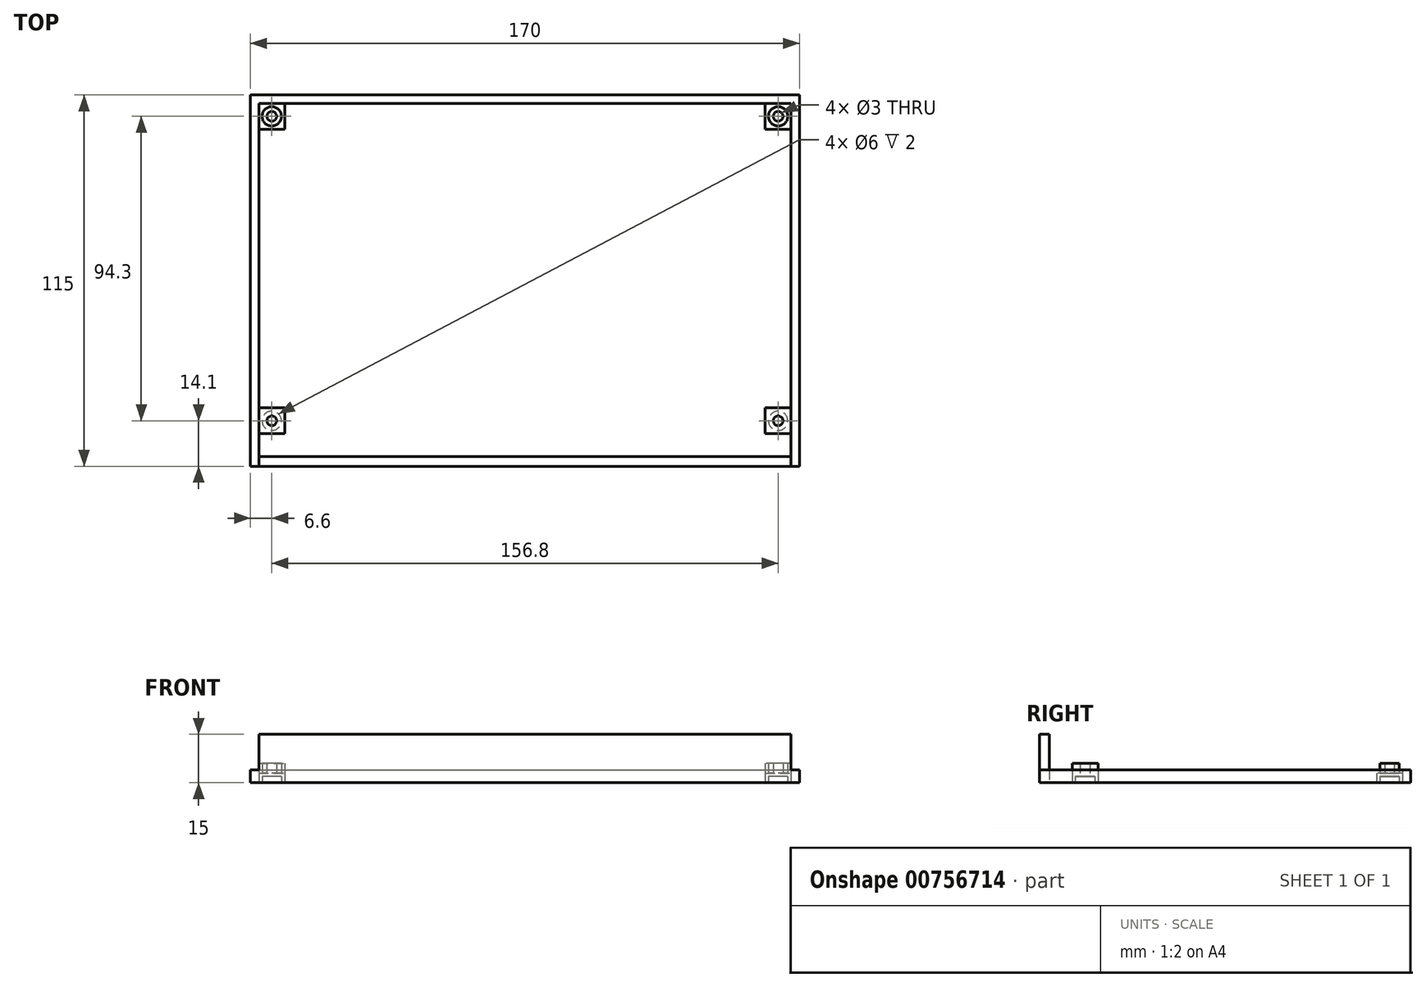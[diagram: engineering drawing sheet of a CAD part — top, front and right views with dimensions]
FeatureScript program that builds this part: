
annotation { "Feature Type Name" : "Feature", "Feature Type Description" : "" }
export const myFeature = defineFeature(function(context is Context, id is Id, definition is map)
    precondition{}
    {
        {
            var Q0;
            Q0=qCreatedBy(makeId("Top.planeOp"),FACE);
            var sketch = newSketch(context, id + "F0", { "sketchPlane" : qUnion([Q0])});
            skLineSegment(sketch, "E0.bottom", {"start": v(0, 0) * mm, "end": v(170, 0) * mm});
            skLineSegment(sketch, "E0.top", {"start": v(0, -115) * mm, "end": v(170, -115) * mm});
            skLineSegment(sketch, "E0.left", {"start": v(0, 0) * mm, "end": v(0, -115) * mm});
            skLineSegment(sketch, "E0.right", {"start": v(170, 0) * mm, "end": v(170, -115) * mm});
            skLineSegment(sketch, "E1", {"start": v(2.6, -115) * mm, "end": v(2.6, -2.6) * mm});
            skLineSegment(sketch, "E2", {"start": v(2.6, -2.6) * mm, "end": v(167.4, -2.6) * mm});
            skLineSegment(sketch, "E3", {"start": v(167.4, -2.6) * mm, "end": v(167.4, -115) * mm});
            skLineSegment(sketch, "E4", {"start": v(0, -67.06) * mm, "end": v(2.6, -67.06) * mm, "construction": true});
            skLineSegment(sketch, "E5", {"start": v(77.9, -2.6) * mm, "end": v(77.9, 0) * mm, "construction": true});
            skLineSegment(sketch, "E6", {"start": v(167.4, -63.68) * mm, "end": v(170, -63.68) * mm, "construction": true});
            skLineSegment(sketch, "E7.bottom", {"start": v(2.6, -2.6) * mm, "end": v(10.6, -2.6) * mm});
            skLineSegment(sketch, "E7.top", {"start": v(2.6, -10.6) * mm, "end": v(10.6, -10.6) * mm});
            skLineSegment(sketch, "E7.left", {"start": v(2.6, -2.6) * mm, "end": v(2.6, -10.6) * mm});
            skLineSegment(sketch, "E7.right", {"start": v(10.6, -2.6) * mm, "end": v(10.6, -10.6) * mm});
            skLineSegment(sketch, "E8.bottom", {"start": v(167.4, -2.6) * mm, "end": v(159.4, -2.6) * mm});
            skLineSegment(sketch, "E8.top", {"start": v(167.4, -10.6) * mm, "end": v(159.4, -10.6) * mm});
            skLineSegment(sketch, "E8.left", {"start": v(167.4, -2.6) * mm, "end": v(167.4, -10.6) * mm});
            skLineSegment(sketch, "E8.right", {"start": v(159.4, -2.6) * mm, "end": v(159.4, -10.6) * mm});
            skLineSegment(sketch, "E9.bottom", {"start": v(167.4, -96.9) * mm, "end": v(159.4, -96.9) * mm});
            skLineSegment(sketch, "E9.top", {"start": v(167.4, -104.9) * mm, "end": v(159.4, -104.9) * mm});
            skLineSegment(sketch, "E9.left", {"start": v(167.4, -96.9) * mm, "end": v(167.4, -104.9) * mm});
            skLineSegment(sketch, "E9.right", {"start": v(159.4, -96.9) * mm, "end": v(159.4, -104.9) * mm});
            skLineSegment(sketch, "E10.bottom", {"start": v(2.6, -96.9) * mm, "end": v(10.6, -96.9) * mm});
            skLineSegment(sketch, "E10.top", {"start": v(2.6, -104.9) * mm, "end": v(10.6, -104.9) * mm});
            skLineSegment(sketch, "E10.left", {"start": v(2.6, -96.9) * mm, "end": v(2.6, -104.9) * mm});
            skLineSegment(sketch, "E10.right", {"start": v(10.6, -96.9) * mm, "end": v(10.6, -104.9) * mm});
            skLineSegment(sketch, "E11", {"start": v(2.6, -112) * mm, "end": v(167.4, -112) * mm});
            skLineSegment(sketch, "E12", {"start": v(167.4, -112) * mm, "end": v(167.4, -115) * mm});
            skLineSegment(sketch, "E13", {"start": v(2.6, -115) * mm, "end": v(2.6, -112) * mm});
            skLineSegment(sketch, "E14", {"start": v(2.6, -2.6) * mm, "end": v(10.6, -10.6) * mm, "construction": true});
            skLineSegment(sketch, "E15", {"start": v(159.4, -2.6) * mm, "end": v(167.4, -10.6) * mm, "construction": true});
            skLineSegment(sketch, "E16", {"start": v(159.4, -96.9) * mm, "end": v(167.4, -104.9) * mm, "construction": true});
            skLineSegment(sketch, "E17", {"start": v(2.6, -96.9) * mm, "end": v(10.6, -104.9) * mm, "construction": true});
            skCircle(sketch, "E18", {"center": v(6.6, -6.6) * mm, "radius": 1.5 * mm});
            skCircle(sketch, "E19", {"center": v(163.4, -6.6) * mm, "radius": 1.5 * mm});
            skCircle(sketch, "E20", {"center": v(163.4, -100.9) * mm, "radius": 1.5 * mm});
            skCircle(sketch, "E21", {"center": v(6.6, -100.9) * mm, "radius": 1.5 * mm});
            skCircle(sketch, "E22", {"center": v(163.4, -6.6) * mm, "radius": 3 * mm});
            skCircle(sketch, "E23", {"center": v(6.6, -6.6) * mm, "radius": 3 * mm});
            skCircle(sketch, "E24", {"center": v(6.6, -100.9) * mm, "radius": 3 * mm});
            skCircle(sketch, "E25", {"center": v(163.4, -100.9) * mm, "radius": 3 * mm});
            skSolve(sketch);
        }
        {
            var Q0;
            Q0=makeQuery(id+"F0.imprint","IMPRINT",FACE,{"disambiguationData":[TD([[makeQuery(id+"F0.imprint","IMPRINT",EDGE,{"derivedFrom":sQuery(id+"F0.wireOp",EDGE,"E0.bottom")}),-1.0]])]});
            extrude(context, id + "F1", {"entities" : qUnion([Q0]), "depth" : 4 * mm, "offsetDistance" : 25 * mm});
        }
        {
            var Q0;
            Q0=makeQuery(id+"F0.imprint","IMPRINT",FACE,{"disambiguationData":[TD([[makeQuery(id+"F0.imprint","IMPRINT",EDGE,{"derivedFrom":sQuery(id+"F0.wireOp",EDGE,"E2")}),-1.0]])]});
            extrude(context, id + "F2", {"entities" : qUnion([Q0]), "operationType" : NewBodyOperationType.ADD, "depth" : 3 * mm, "offsetDistance" : 25 * mm});
        }
        {
            var Q0;
            Q0=makeQuery(id+"F0.imprint","IMPRINT",FACE,{"disambiguationData":[TD([[makeQuery(id+"F0.imprint","IMPRINT",EDGE,{"derivedFrom":sQuery(id+"F0.wireOp",EDGE,"E10.bottom")}),-1.0]])]});
            var Q1;
            Q1=makeQuery(id+"F0.imprint","IMPRINT",FACE,{"disambiguationData":[TD([[makeQuery(id+"F0.imprint","IMPRINT",EDGE,{"derivedFrom":sQuery(id+"F0.wireOp",EDGE,"E21")}),-1.0]])]});
            var Q2;
            Q2=makeQuery(id+"F0.imprint","IMPRINT",FACE,{"disambiguationData":[TD([[makeQuery(id+"F0.imprint","IMPRINT",EDGE,{"derivedFrom":sQuery(id+"F0.wireOp",EDGE,"E9.bottom")}),1.0]])]});
            var Q3;
            Q3=makeQuery(id+"F0.imprint","IMPRINT",FACE,{"disambiguationData":[TD([[makeQuery(id+"F0.imprint","IMPRINT",EDGE,{"derivedFrom":sQuery(id+"F0.wireOp",EDGE,"E20")}),-1.0]])]});
            var Q4;
            Q4=makeQuery(id+"F0.imprint","IMPRINT",FACE,{"disambiguationData":[TD([[makeQuery(id+"F0.imprint","IMPRINT",EDGE,{"derivedFrom":sQuery(id+"F0.wireOp",EDGE,"E8.bottom")}),1.0]])]});
            var Q5;
            Q5=makeQuery(id+"F0.imprint","IMPRINT",FACE,{"disambiguationData":[TD([[makeQuery(id+"F0.imprint","IMPRINT",EDGE,{"derivedFrom":sQuery(id+"F0.wireOp",EDGE,"E19")}),-1.0]])]});
            var Q6;
            Q6=makeQuery(id+"F0.imprint","IMPRINT",FACE,{"disambiguationData":[TD([[makeQuery(id+"F0.imprint","IMPRINT",EDGE,{"derivedFrom":sQuery(id+"F0.wireOp",EDGE,"E7.bottom")}),-1.0]])]});
            var Q7;
            Q7=makeQuery(id+"F0.imprint","IMPRINT",FACE,{"disambiguationData":[TD([[makeQuery(id+"F0.imprint","IMPRINT",EDGE,{"derivedFrom":sQuery(id+"F0.wireOp",EDGE,"E18")}),-1.0]])]});
            extrude(context, id + "F3", {"entities" : qUnion([Q0, Q1, Q2, Q3, Q4, Q5, Q6, Q7]), "operationType" : NewBodyOperationType.ADD, "depth" : 6 * mm, "offsetDistance" : 25 * mm});
        }
        {
            var Q0;
            Q0=makeQuery(id+"F0.imprint","IMPRINT",FACE,{"disambiguationData":[TD([[makeQuery(id+"F0.imprint","IMPRINT",EDGE,{"derivedFrom":sQuery(id+"F0.wireOp",EDGE,"E11")}),-1.0]])]});
            extrude(context, id + "F4", {"entities" : qUnion([Q0]), "operationType" : NewBodyOperationType.ADD, "depth" : 15 * mm, "offsetDistance" : 25 * mm});
        }
        {
            var Q0;
            Q0=makeQuery(id+"F0.imprint","IMPRINT",FACE,{"disambiguationData":[TD([[makeQuery(id+"F0.imprint","IMPRINT",EDGE,{"derivedFrom":sQuery(id+"F0.wireOp",EDGE,"E19")}),-1.0]])]});
            var Q1;
            Q1=makeQuery(id+"F0.imprint","IMPRINT",FACE,{"disambiguationData":[TD([[makeQuery(id+"F0.imprint","IMPRINT",EDGE,{"derivedFrom":sQuery(id+"F0.wireOp",EDGE,"E18")}),-1.0]])]});
            var Q2;
            Q2=makeQuery(id+"F0.imprint","IMPRINT",FACE,{"disambiguationData":[TD([[makeQuery(id+"F0.imprint","IMPRINT",EDGE,{"derivedFrom":sQuery(id+"F0.wireOp",EDGE,"E21")}),-1.0]])]});
            var Q3;
            Q3=makeQuery(id+"F0.imprint","IMPRINT",FACE,{"disambiguationData":[TD([[makeQuery(id+"F0.imprint","IMPRINT",EDGE,{"derivedFrom":sQuery(id+"F0.wireOp",EDGE,"E20")}),-1.0]])]});
            extrude(context, id + "F5", {"entities" : qUnion([Q0, Q1, Q2, Q3]), "operationType" : NewBodyOperationType.REMOVE, "depth" : 2 * mm, "offsetDistance" : 25 * mm});
        }
        {
            var Q0;
            {var subQ0=sQuery(id+"F0.wireOp",EDGE,"E13");var subQ1=sQuery(id+"F0.wireOp",EDGE,"E12");var subQ2=sQuery(id+"F0.wireOp",EDGE,"E11");var subQ3=sQuery(id+"F0.wireOp",EDGE,"E0.top");var subQ4=sQuery(id+"F0.wireOp",EDGE,"E10.right");var subQ5=sQuery(id+"F0.wireOp",EDGE,"E10.left");var subQ6=sQuery(id+"F0.wireOp",EDGE,"E10.top");var subQ7=sQuery(id+"F0.wireOp",EDGE,"E10.bottom");var subQ8=sQuery(id+"F0.wireOp",EDGE,"E9.right");var subQ9=sQuery(id+"F0.wireOp",EDGE,"E9.left");var subQ10=sQuery(id+"F0.wireOp",EDGE,"E9.top");var subQ11=sQuery(id+"F0.wireOp",EDGE,"E9.bottom");var subQ12=sQuery(id+"F0.wireOp",EDGE,"E8.right");var subQ13=sQuery(id+"F0.wireOp",EDGE,"E8.left");var subQ14=sQuery(id+"F0.wireOp",EDGE,"E8.top");var subQ15=sQuery(id+"F0.wireOp",EDGE,"E8.bottom");var subQ16=sQuery(id+"F0.wireOp",EDGE,"E7.right");var subQ17=sQuery(id+"F0.wireOp",EDGE,"E7.left");var subQ18=sQuery(id+"F0.wireOp",EDGE,"E7.top");var subQ19=sQuery(id+"F0.wireOp",EDGE,"E7.bottom");var subQ20=sQuery(id+"F0.wireOp",EDGE,"E3");var subQ21=sQuery(id+"F0.wireOp",EDGE,"E2");var subQ22=sQuery(id+"F0.wireOp",EDGE,"E1");Q0=makeQuery(id+"F4.boolean.opBoolean","MERGE",FACE,{"derivedFrom":[makeQuery(id+"F3.boolean.opBoolean","MERGE",FACE,{"derivedFrom":[makeQuery(id+"F2.boolean.opBoolean","MERGE",FACE,{"derivedFrom":[makeQuery(id+"F1.opExtrude","CAP_FACE",FACE,{"disambiguationData":[OSD([sQuery(id+"F0.wireOp",EDGE,"E0.bottom"),subQ3,sQuery(id+"F0.wireOp",EDGE,"E0.left"),sQuery(id+"F0.wireOp",EDGE,"E0.right"),subQ22,subQ21,subQ20,subQ19,subQ17,subQ15,subQ13,subQ9,subQ5,subQ1,subQ0])],"isStart":true}),makeQuery(id+"F2.opExtrude","CAP_FACE",FACE,{"disambiguationData":[OSD([subQ22,subQ21,subQ20,subQ18,subQ16,subQ14,subQ12,subQ11,subQ10,subQ8,subQ7,subQ6,subQ4,subQ2])],"isStart":true})]}),makeQuery(id+"F3.opExtrude","CAP_FACE",FACE,{"disambiguationData":[OSD([subQ19,subQ18,subQ17,subQ16,sQuery(id+"F0.wireOp",EDGE,"E18")])],"isStart":true}),makeQuery(id+"F3.opExtrude","CAP_FACE",FACE,{"disambiguationData":[OSD([subQ15,subQ14,subQ13,subQ12,sQuery(id+"F0.wireOp",EDGE,"E19")])],"isStart":true}),makeQuery(id+"F3.opExtrude","CAP_FACE",FACE,{"disambiguationData":[OSD([subQ11,subQ10,subQ9,subQ8,sQuery(id+"F0.wireOp",EDGE,"E20")])],"isStart":true}),makeQuery(id+"F3.opExtrude","CAP_FACE",FACE,{"disambiguationData":[OSD([subQ7,subQ6,subQ5,subQ4,sQuery(id+"F0.wireOp",EDGE,"E21")])],"isStart":true})]}),makeQuery(id+"F4.opExtrude","CAP_FACE",FACE,{"disambiguationData":[OSD([subQ3,subQ2,subQ1,subQ0])],"isStart":true})]});}
            var sketch = newSketch(context, id + "F6", { "sketchPlane" : qUnion([Q0])});
            skLineSegment(sketch, "E26", {"start": v(163.4, 100.9) * mm, "end": v(163.4, 82.08) * mm, "construction": true});
            skLineSegment(sketch, "E27", {"start": v(6.6, 100.9) * mm, "end": v(6.6, 82.08) * mm, "construction": true});
            skLineSegment(sketch, "E28", {"start": v(0, 82.08) * mm, "end": v(170, 82.08) * mm, "construction": true});
            skText(sketch, "E29", { "text": "Growth-In-A-Box", "fontName": "AllertaStencil-Regular.ttf"});
            skLineSegment(sketch, "E30", {"start": v(170, 47.08) * mm, "end": v(0, 47.08) * mm, "construction": true});
            skText(sketch, "E31", { "text": "Controller", "fontName": "AllertaStencil-Regular.ttf"});
            skText(sketch, "E32", { "text": "By Marcus, Rasmus\n& Soeren", "fontName": "AllertaStencil-Regular.ttf"});
            skLineSegment(sketch, "E33", {"start": v(0, 25) * mm, "end": v(170, 25) * mm, "construction": true});
            const initialGuessF6  = {"E29": [0.0066, 0.08208, 1, 0, 0.01292], "E31": [0.01237, 0.04708, 1, 0, 0.02], "E32": [0.01803, 0.025, 1, 0, 0.01017]};
            skSetInitialGuess(sketch, initialGuessF6);
            skSolve(sketch);
        }
        {
            var Q0;
            Q0=qSketchRegion(id+"F6",true);
            extrude(context, id + "F7", {"entities" : qUnion([Q0]), "operationType" : NewBodyOperationType.REMOVE, "oppositeDirection" : true, "depth" : 25 * mm, "offsetDistance" : 25 * mm});
        }
    });
